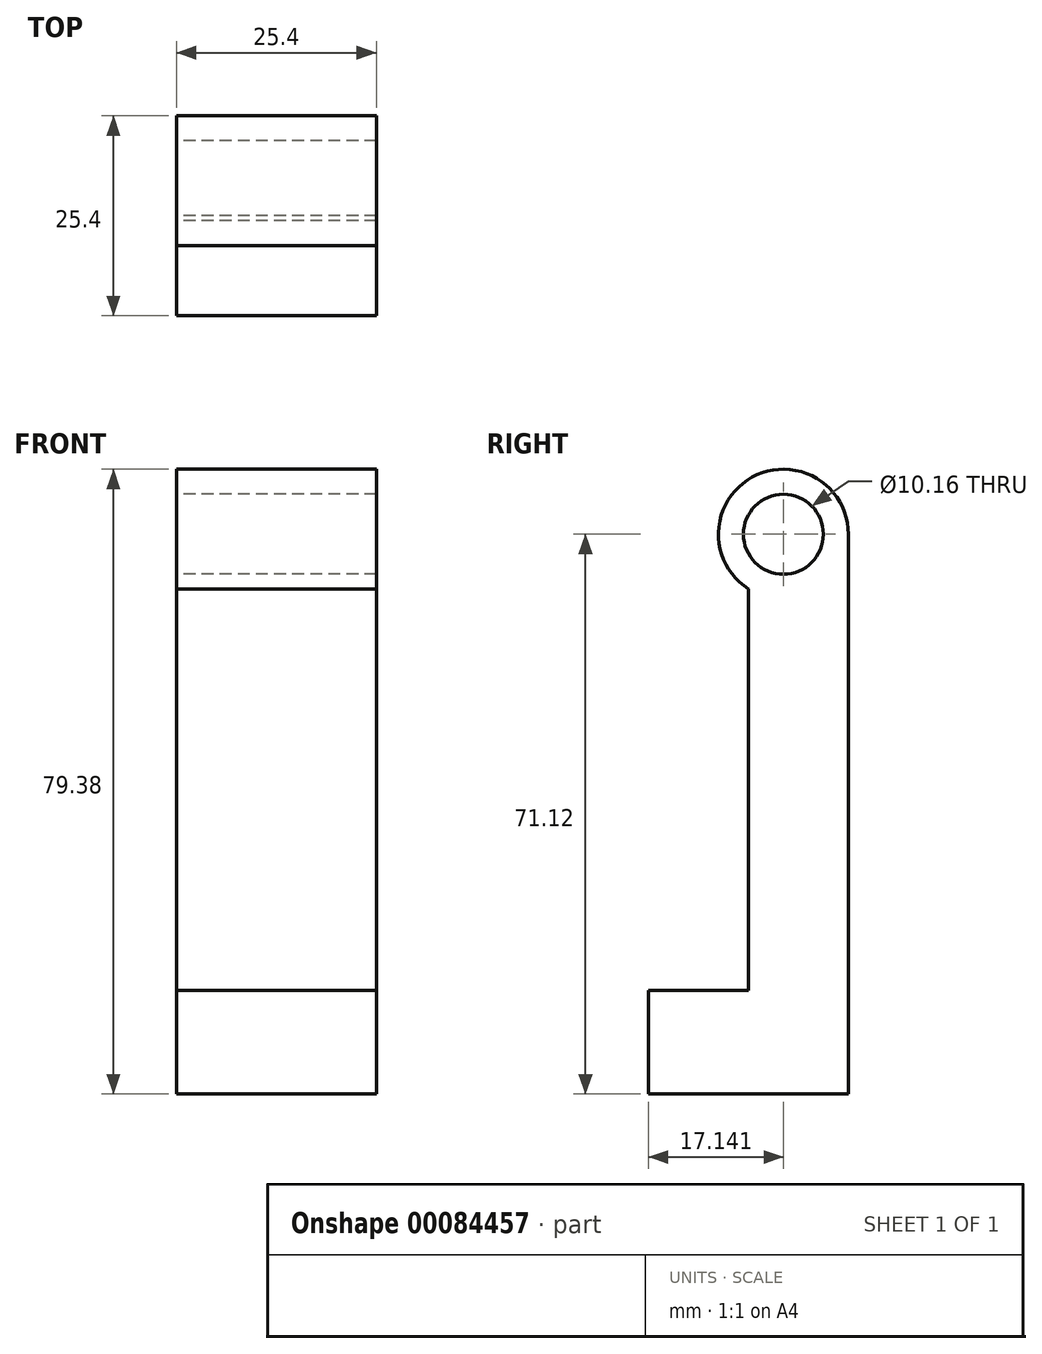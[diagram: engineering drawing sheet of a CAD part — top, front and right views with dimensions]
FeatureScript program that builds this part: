
annotation { "Feature Type Name" : "Feature", "Feature Type Description" : "" }
export const myFeature = defineFeature(function(context is Context, id is Id, definition is map)
    precondition{}
    {
        {
            var Q0;
            Q0=qCreatedBy(makeId("Top.planeOp"),FACE);
            var sketch = newSketch(context, id + "F0", { "sketchPlane" : qUnion([Q0])});
            skLineSegment(sketch, "E0.bottom", {"start": v(-17.1, 4.46) * mm, "end": v(8.3, 4.46) * mm});
            skLineSegment(sketch, "E0.top", {"start": v(-17.1, -20.94) * mm, "end": v(8.3, -20.94) * mm});
            skLineSegment(sketch, "E0.left", {"start": v(-17.1, 4.46) * mm, "end": v(-17.1, -20.94) * mm});
            skLineSegment(sketch, "E0.right", {"start": v(8.3, 4.46) * mm, "end": v(8.3, -20.94) * mm});
            skLineSegment(sketch, "E1", {"start": v(-4.4, -8.24) * mm, "end": v(8.3, -8.24) * mm});
            skPoint(sketch, "E1.startSnap0", {"position": v(8.3, -8.24) * mm});
            skPoint(sketch, "E1.startSnap1", {"position": v(-4.4, 4.46) * mm});
            skLineSegment(sketch, "E2", {"start": v(8.3, -8.24) * mm, "end": v(-17.1, -8.24) * mm});
            skSolve(sketch);
        }
        {
            var Q0;
            {var subQ4=sQuery(id+"F0.wireOp",EDGE,"E0.top");Q0=makeQuery(id+"F0.imprint","IMPRINT",FACE,{"disambiguationData":[TD([[makeQuery(id+"F0.imprint","IMPRINT",EDGE,{"derivedFrom":subQ4}),1.0]])]});}
            extrude(context, id + "F1", {"entities" : qUnion([Q0]), "depth" : 13.15 * mm});
        }
        {
            var Q0;
            {var subQ4=sQuery(id+"F0.wireOp",EDGE,"E0.bottom");Q0=makeQuery(id+"F0.imprint","IMPRINT",FACE,{"disambiguationData":[TD([[makeQuery(id+"F0.imprint","IMPRINT",EDGE,{"derivedFrom":subQ4}),-1.0]])]});}
            extrude(context, id + "F2", {"entities" : qUnion([Q0]), "operationType" : NewBodyOperationType.ADD, "depth" : 71.12 * mm});
        }
        {
            var Q0;
            {var subQ0=sQuery(id+"F0.wireOp",EDGE,"E0.right");Q0=makeQuery(id+"F2.boolean.opBoolean","MERGE",FACE,{"derivedFrom":[makeQuery(id+"F1.opExtrude","SWEPT_FACE",FACE,{"disambiguationData":[OSD([subQ0])]}),makeQuery(id+"F2.opExtrude","SWEPT_FACE",FACE,{"disambiguationData":[OSD([subQ0])]})]});}
            var sketch = newSketch(context, id + "F3", { "sketchPlane" : qUnion([Q0])});
            skCircle(sketch, "E3", {"center": v(-3.8, 71.12) * mm, "radius": 8.26 * mm});
            skPoint(sketch, "E4", {"position": v(-1.89, 71.12) * mm});
            skSolve(sketch);
        }
        {
            var Q0;
            {var subQ0=sQuery(id+"F3.wireOp",EDGE,"E3");var subQ1=sQuery(id+"F0.wireOp",EDGE,"E0.right");var subQ2=makeQuery(id+"F2.opExtrude","CAP_EDGE",EDGE,{"disambiguationData":[OSD([subQ1])],"isStart":false});var subQ3=makeQuery(id+"F3.imprint","INTERSECT",VERTEX,{"derivedFrom":[subQ2,subQ0]});Q0=makeQuery(id+"F3.imprint","IMPRINT",FACE,{"disambiguationData":[TD([[makeQuery(id+"F3.imprint","IMPRINT",EDGE,{"disambiguationData":[TD([[subQ3,-1.0]])],"derivedFrom":subQ0}),1.0]])]});}
            extrude(context, id + "F4", {"entities" : qUnion([Q0]), "operationType" : NewBodyOperationType.ADD, "oppositeDirection" : true, "depth" : 25.4 * mm});
        }
        {
            var Q0;
            Q0=sQuery(id+"F3.wireOp",VERTEX,"E3.center");
            var Q1;
            Q1=makeQuery(id+"F1.opExtrude","SWEPT_BODY",BODY,{"disambiguationData":[OSD([sQuery(id+"F0.wireOp",EDGE,"E0.top"),sQuery(id+"F0.wireOp",EDGE,"E0.left"),sQuery(id+"F0.wireOp",EDGE,"E0.right"),sQuery(id+"F0.wireOp",EDGE,"E2")])]});
            hole(context, id + "F5", {"style" : HoleStyle.SIMPLE, "endStyle" : HoleEndStyle.THROUGH, "holeDiameter" : 10.16 * mm, "locations" : qUnion([Q0]), "scope" : qUnion([Q1]), "isTappedThrough" : true});
        }
    });
